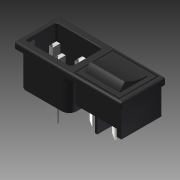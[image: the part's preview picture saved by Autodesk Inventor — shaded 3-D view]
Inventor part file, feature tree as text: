
AUTODESK INVENTOR PART (.ipt)
format: ipt  version: 2015 (Build 190159000, 159)  size: 409,088 bytes
history: native  units: mm
features: extrude x13, fillet x6, projected_geometry x2, pattern_linear x1, chamfer x1
ambient origin geometry x8: Origin, YZ Plane, XZ Plane, XY Plane, X Axis, Y Axis, Z Axis, Center Point
bodies: Solid1 (feature_tree)
feature tree (23):
  extrude  "Extrusión1"  Depth=57.5mm
  extrude  "Extrusión3"  Depth=24.0mm
  fillet  "Empalme1"  Radius=54.9mm
  extrude  "Extrusión4"  Depth=21.3mm
  extrude  "Extrusión5"  Depth=3.2mm TaperAngle=0.0deg
  extrude  "Extrusión6"  Depth=27.0mm
  extrude  "Extrusión7"  Depth=21.3mm
  pattern_linear  "Patrón rectangular1"  Spacing1=17.8mm  [1 undecoded]
  extrude  "Extrusión8"  Depth=4.0mm
  extrude  "Extrusión9"  Depth=24.4mm
  extrude  "Extrusión10"  Depth=11.2mm TaperAngle=0.0deg
  fillet  "Empalme2"  Radius=2.5mm
  fillet  "Empalme3"  Radius=3.75mm
  extrude  "Extrusión11"  Depth=1.25mm
  fillet  "Empalme4"  Radius=7.8mm
  fillet  "Empalme5"  Radius=0.8mm
  chamfer  "Chaflán1"  Distance=4.7mm
  extrude  "Extrusión12"  Depth=7.8mm TaperAngle=0.0deg
  extrude  "Extrusión13"  Depth=20.0mm
  extrude  "Extrusión14"  Depth=20.0mm
  fillet  "Empalme6"  Radius=12.5mm
  projected_geometry  "Contorno proyectado1"
  projected_geometry  "Contorno proyectado2"
note: 1 required parameter value undecoded (feature->parameter linkage not recoverable at this tier; creation-order binding heuristic only, values carry confidence <= 0.55)
